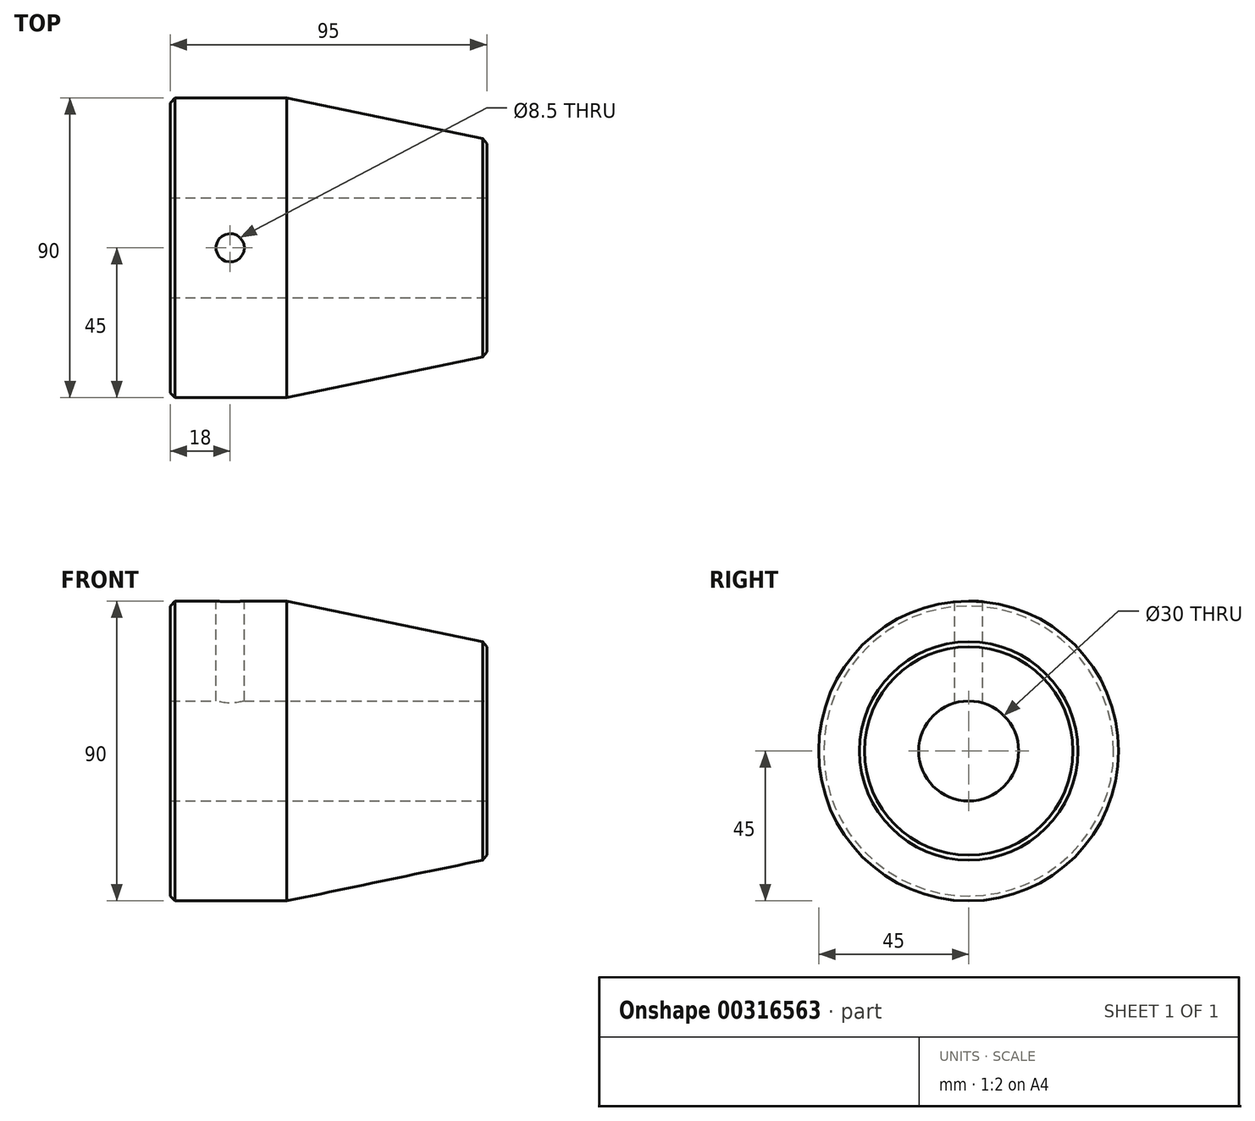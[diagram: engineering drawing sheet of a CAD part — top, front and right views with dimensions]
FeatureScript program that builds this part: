
annotation { "Feature Type Name" : "Feature", "Feature Type Description" : "" }
export const myFeature = defineFeature(function(context is Context, id is Id, definition is map)
    precondition{}
    {
        {
            var Q0;
            Q0=qCreatedBy(makeId("Right.planeOp"),FACE);
            var sketch = newSketch(context, id + "F0", { "sketchPlane" : qUnion([Q0])});
            skCircle(sketch, "E0", {"center": v(0, 0) * mm, "radius": 45 * mm});
            skSolve(sketch);
        }
        {
            var Q0;
            Q0=qCreatedBy(makeId("Right.planeOp"),FACE);
            cPlane(context, id + "F1", {"entities" : qUnion([Q0]), "cplaneType" : CPlaneType.OFFSET, "offset" : 95 * mm, "width" : 150 * mm, "height" : 150 * mm});
        }
        {
            var Q0;
            Q0=qCreatedBy(id+"F1.planeOp",FACE);
            var sketch = newSketch(context, id + "F2", { "sketchPlane" : qUnion([Q0])});
            skCircle(sketch, "E1", {"center": v(0, 0) * mm, "radius": 32.5 * mm});
            skSolve(sketch);
        }
        {
            var Q0;
            Q0=makeQuery(id+"F0.imprint","IMPRINT",FACE,{"disambiguationData":[TD([[makeQuery(id+"F0.imprint","IMPRINT",EDGE,{"derivedFrom":sQuery(id+"F0.wireOp",EDGE,"E0")}),1.0]])]});
            extrude(context, id + "F3", {"entities" : qUnion([Q0]), "depth" : 35 * mm});
        }
        {
            var Q0;
            Q0=makeQuery(id+"F3.opExtrude","CAP_FACE",FACE,{"disambiguationData":[OSD([sQuery(id+"F0.wireOp",EDGE,"E0")])],"isStart":false});
            var sketch = newSketch(context, id + "F4", { "sketchPlane" : qUnion([Q0])});
            skCircle(sketch, "E2.0", {"center": v(0, 0) * mm, "radius": 45 * mm});
            skSolve(sketch);
        }
        {
            var Q1;
            Q1=makeQuery(id+"F4.imprint","IMPRINT",FACE,{"disambiguationData":[TD([[makeQuery(id+"F4.imprint","IMPRINT",EDGE,{"derivedFrom":sQuery(id+"F4.wireOp",EDGE,"E2.0")}),1.0]])]});
            var Q2;
            Q2=makeQuery(id+"F2.imprint","IMPRINT",FACE,{"disambiguationData":[TD([[makeQuery(id+"F2.imprint","IMPRINT",EDGE,{"derivedFrom":sQuery(id+"F2.wireOp",EDGE,"E1")}),1.0]])]});
            loft(context, id + "F5", {"operationType" : NewBodyOperationType.ADD, "sheetProfilesArray" : [{ "sheetProfileEntities" : qUnion([Q1]) }, { "sheetProfileEntities" : qUnion([Q2]) }]});
        }
        {
            var Q0;
            Q0=qCreatedBy(makeId("Top.planeOp"),FACE);
            cPlane(context, id + "F6", {"entities" : qUnion([Q0]), "cplaneType" : CPlaneType.OFFSET, "offset" : 45 * mm, "width" : 150 * mm, "height" : 150 * mm});
        }
        {
            var Q0;
            Q0=qCreatedBy(id+"F6.planeOp",FACE);
            var sketch = newSketch(context, id + "F7", { "sketchPlane" : qUnion([Q0])});
            skLineSegment(sketch, "E3", {"start": v(0, 0) * mm, "end": v(18, 0) * mm, "construction": true});
            skPoint(sketch, "E4", {"position": v(18, 0) * mm});
            skSolve(sketch);
        }
        {
            var Q0;
            Q0=makeQuery(id+"F5.opLoft","CAP_FACE",FACE,{"disambiguationData":[OSD([makeQuery(id+"F2.imprint","IMPRINT",FACE,{"disambiguationData":[TD([[makeQuery(id+"F2.imprint","IMPRINT",EDGE,{"derivedFrom":sQuery(id+"F2.wireOp",EDGE,"E1")}),1.0]])]})])],"isStart":true});
            var sketch = newSketch(context, id + "F8", { "sketchPlane" : qUnion([Q0])});
            skPoint(sketch, "E5", {"position": v(0, 0) * mm});
            skSolve(sketch);
        }
        {
            var Q0;
            Q0=sQuery(id+"F8.wireOp",VERTEX,"E5");
            var Q1;
            Q1=makeQuery(id+"F3.opExtrude","SWEPT_BODY",BODY,{"disambiguationData":[OSD([sQuery(id+"F0.wireOp",EDGE,"E0")])]});
            hole(context, id + "F9", {"style" : HoleStyle.SIMPLE, "endStyle" : HoleEndStyle.THROUGH, "standardTappedOrClearance" : lookupTablePath({ "standard" : "ISO", "size" : "30", "type" : "Drilled" }), "standardBlindInLast" : lookupTablePath({ "standard" : "ISO", "size" : "30", "type" : "Drilled" }), "holeDiameter" : 30 * mm, "tappedDepth" : 24 * mm, "tapClearance" : 3, "locations" : qUnion([Q0]), "scope" : qUnion([Q1])});
        }
        {
            var Q0;
            Q0=sQuery(id+"F7.wireOp",VERTEX,"E4");
            var Q1;
            Q1=makeQuery(id+"F3.opExtrude","SWEPT_BODY",BODY,{"disambiguationData":[OSD([sQuery(id+"F0.wireOp",EDGE,"E0")])]});
            hole(context, id + "F10", {"style" : HoleStyle.SIMPLE, "endStyle" : HoleEndStyle.BLIND, "standardTappedOrClearance" : lookupTablePath({ "standard" : "ISO", "engagement" : "75%", "pitch" : "1.5 mm", "size" : "M10", "type" : "Tapped" }), "standardBlindInLast" : lookupTablePath({ "standard" : "ISO", "engagement" : "75%", "pitch" : "1.5 mm", "size" : "M10", "type" : "Tapped" }), "holeDiameter" : 8.5 * mm, "showTappedDepth" : true, "holeDepth" : 45 * mm, "tappedDepth" : 40.5 * mm, "tapClearance" : 3, "locations" : qUnion([Q0]), "scope" : qUnion([Q1]), "majorDiameter" : 10 * mm});
        }
        {
            var Q0;
            Q0=makeQuery(id+"F9.hole-0.boolean.opBoolean","COPY",EDGE,{"derivedFrom":makeQuery(id+"F9.hole-0.opRevolve","SWEPT_EDGE",EDGE,{"disambiguationData":[OSD([sQuery(id+"F9.hole-0.sketch.wireOp",EDGE,"core_line_2"),sQuery(id+"F9.hole-0.sketch.wireOp",EDGE,"core_line_3")])]})});
            var Q1;
            Q1=makeQuery(id+"F5.opLoft","MID_CAP_EDGE",EDGE,{"disambiguationData":[OSD([sQuery(id+"F2.wireOp",EDGE,"E1"),sQuery(id+"F4.wireOp",EDGE,"E2.0")])],"capPos":1.0});
            var Q2;
            Q2=makeQuery(id+"F3.opExtrude","CAP_EDGE",EDGE,{"disambiguationData":[OSD([sQuery(id+"F0.wireOp",EDGE,"E0")])],"isStart":true});
            var Q3;
            Q3=makeQuery(id+"F9.hole-0.boolean.opBoolean","INTERSECT",EDGE,{"derivedFrom":[makeQuery(id+"F3.opExtrude","CAP_FACE",FACE,{"disambiguationData":[OSD([sQuery(id+"F0.wireOp",EDGE,"E0")])],"isStart":true}),makeQuery(id+"F9.hole-0.opRevolve","SWEPT_FACE",FACE,{"disambiguationData":[OSD([sQuery(id+"F9.hole-0.sketch.wireOp",EDGE,"core_line_2")])]})]});
            chamfer(context, id + "F11", {"entities" : qUnion([Q0, Q1, Q2, Q3]), "width" : 1.5 * mm, "tangentPropagation" : true});
        }
    });
